# Revit family: HVAC_HeatPumpBW_Enertech_CTC-EcoPart-600M
name_source: partatom
category: Specialty Equipment
units: mm (PartAtom-declared; Revit-internal decimal feet)

## family parameters
Always vertical = No
Cut with Voids When Loaded = No
OmniClass Number = 23.75.00.00
OmniClass Title = Climate Control (HVAC)
Part Type = Normal
Room Calculation Point = No
Round Connector Dimension = Use Diameter
Shared = No
Work Plane-Based = No

## types (2) — shared parameters
AirFlow max (m3/h) = 0
AirFlow nominal (m3/h) = 0
AssetType = Fixed
BIMObjectName = HVAC_HeatPumpBW_Enertech_CTC-EcoPart-600M
Brand = CTC
BrineSystem_Min_MaxPressure = 0.2 - 3.0
Capacity = Variable
Category = Heat pumps, Geothermal
Color = white
Description = The CTC EcoPart 600M is speed-controlled, compact geothermal heat pumps without control and hot water preparation. To fit most properties, the CTC EcoPart 600M is available in two models.
DurationUnit = Year
ElectricalDeviceNominalPower = 0 W
EnergyClassHeatingWithControl W35 = A+++
EnergyClassHeatingWithControl W55 = A+++
EnergyClassHeatingWithoutControl W35 = A+++
EnergyClassHeatingWithoutControl W55 = A+++
HasProtectiveEarth = Yes
IP_Code = IP X1
IfcExportAs = IfcElectricalDeviceCommon
IfcExportType = HEATER
KvsValueProduct = 4.7
Manufacturer = CTC AB
ManufacturerCountry = Sweden
ManufacturerName = CTC AB
ManufacturerURL = https://ctc.se
Material = Steel
MaxOperatingPressureThermalStore = 6
NBSDescription = Air to water heat pumps
NBSReference = 90-40-40/320
Name = CTC-EcoPart-600M
NominalCurrent = 0 A
NominalDepth = 673 mm  [stored 2.20801 ft]
NominalFrequencyRange = 50 Hz
NominalHeight = 775 mm  [stored 2.54265 ft]
NominalVoltage = 400 V
NominalWidth = 596 mm  [stored 1.95538 ft]
NumberOfPoles = 3
PhaseAngle = 0.00°
PowerFactor = 0 W
ProductInformation = The CTC EcoPart 600M is speed-controlled, compact geothermal heat pumps without control and hot water preparation. To fit most properties, the CTC EcoPart 600M is available in two models.
PumpMainMaterial = Steel - White
RatedVoltage = 1200 V
RefrigerantType = R407C
Revision = 2
SCOPCold W35 = 5.5
SCOPWarm W35 = 5.2
Shape = Rectangular
Size = 673x596x775
Touchscreen = no
UNSPSCCode = 40101806
URL = https://ctc-heating.com
Uniclass2 = Pr_40_70_65
Uniclass2015Description = Preparation catering equipment
Uniclass2015Reference = Pr_40_70_65
UsageCurrent = 0 A
Version = 2
VersionDate = 14/05/2024
WarrantyDurationUnit = Year
WaterVolumeHeathingSystem = 4.1
zero-valued in all types: Cost, Default Elevation

## per-type parameters (varying)
- CTC EcoPart 612M - 400V3N: CO2Equivalent=4.258; COP_max: W35 & B 0=5 W; COP_max: W35 & B 10=6 W; COP_max: W35 & B 5=6 W; COP_min: W35 & B 0=7 W; COP_min: W35 & B 10=9 W; COP_min: W35 & B 5=8 W; EANNumber=7333077091736; GroupFuse=10; InPutPower_max: W35 & B 0=2420 W; InPutPower_max: W35 & B 10=2340 W; InPutPower_max: W35 & B 5=2340 W; InPutPower_min: W35 & B 0=330 W; InPutPower_min: W35 & B 10=310 W; InPutPower_min: W35 & B 5=340 W; MaxStartingCurrent=2.3; Model=CTC EcoPart 612M; ModelNumber=588600001; RatedCurrent=10 A; RatedHeatOutputCold Pdesigh W35=11000 W; RatedHeatOutputCold Pdesigh W55=7000 W; RatedHeatOutputModerate Pdesigh W35=10000 W; RatedHeatOutputModerate Pdesigh W55=7000 W; RatedHeatOutputWarm Pdesigh W35=8000 W; RatedHeatOutputWarm Pdesigh W55=10000 W; RefrigerantQuantity=2.4; SCOPCold W55=4.3; SCOPModerate W35=5.4; SCOPModerate W55=4.1; SCOPWarm W55=4.1; Sound pressureLPA 1m=34; SoundPowerLWA=39; SpecifiedOutput_max: W35 & B 0=12140 W; SpecifiedOutput_max: W35 & B 10=13490 W; SpecifiedOutput_max: W35 & B 5=13110 W; SpecifiedOutput_min: W35 & B 0=2270 W; SpecifiedOutput_min: W35 & B 10=2920 W; SpecifiedOutput_min: W35 & B 5=2650 W; Weight=170
- CTC EcoPart 616M - 400V3N: CO2Equivalent=3.903; COP_max: W35 & B 0=4 W; COP_max: W35 & B 10=4 W; COP_max: W35 & B 5=4 W; COP_min: W35 & B 0=5 W; COP_min: W35 & B 10=6 W; COP_min: W35 & B 5=5 W; EANNumber=7333077091743; GroupFuse=13; InPutPower_max: W35 & B 0=4190 W; InPutPower_max: W35 & B 10=4400 W; InPutPower_max: W35 & B 5=4370 W; InPutPower_min: W35 & B 0=900 W; InPutPower_min: W35 & B 10=910 W; InPutPower_min: W35 & B 5=910 W; MaxStartingCurrent=1.8; Model=CTC EcoPart 616M; ModelNumber=588600002; RatedCurrent=12 A; RatedHeatOutputCold Pdesigh W35=16000 W; RatedHeatOutputCold Pdesigh W55=16000 W; RatedHeatOutputModerate Pdesigh W35=16000 W; RatedHeatOutputModerate Pdesigh W55=16000 W; RatedHeatOutputWarm Pdesigh W35=16000 W; RatedHeatOutputWarm Pdesigh W55=16000 W; RefrigerantQuantity=2.2; SCOPCold W55=4.2; SCOPModerate W35=5.2; SCOPModerate W55=4.0; SCOPWarm W55=4.0; Sound pressureLPA 1m=37; SoundPowerLWA=42; SpecifiedOutput_max: W35 & B 0=15600 W; SpecifiedOutput_max: W35 & B 10=16970 W; SpecifiedOutput_max: W35 & B 5=16520 W; SpecifiedOutput_min: W35 & B 0=4200 W; SpecifiedOutput_min: W35 & B 10=5520 W; SpecifiedOutput_min: W35 & B 5=4900 W; Weight=172

note: [stored X ft] marks values corroborated as IEEE doubles in the binary element streams (Revit-internal decimal feet)

## geometry (parser evidence)
native form markers: Sweep x3
no freeform markers — native parametric forms only
